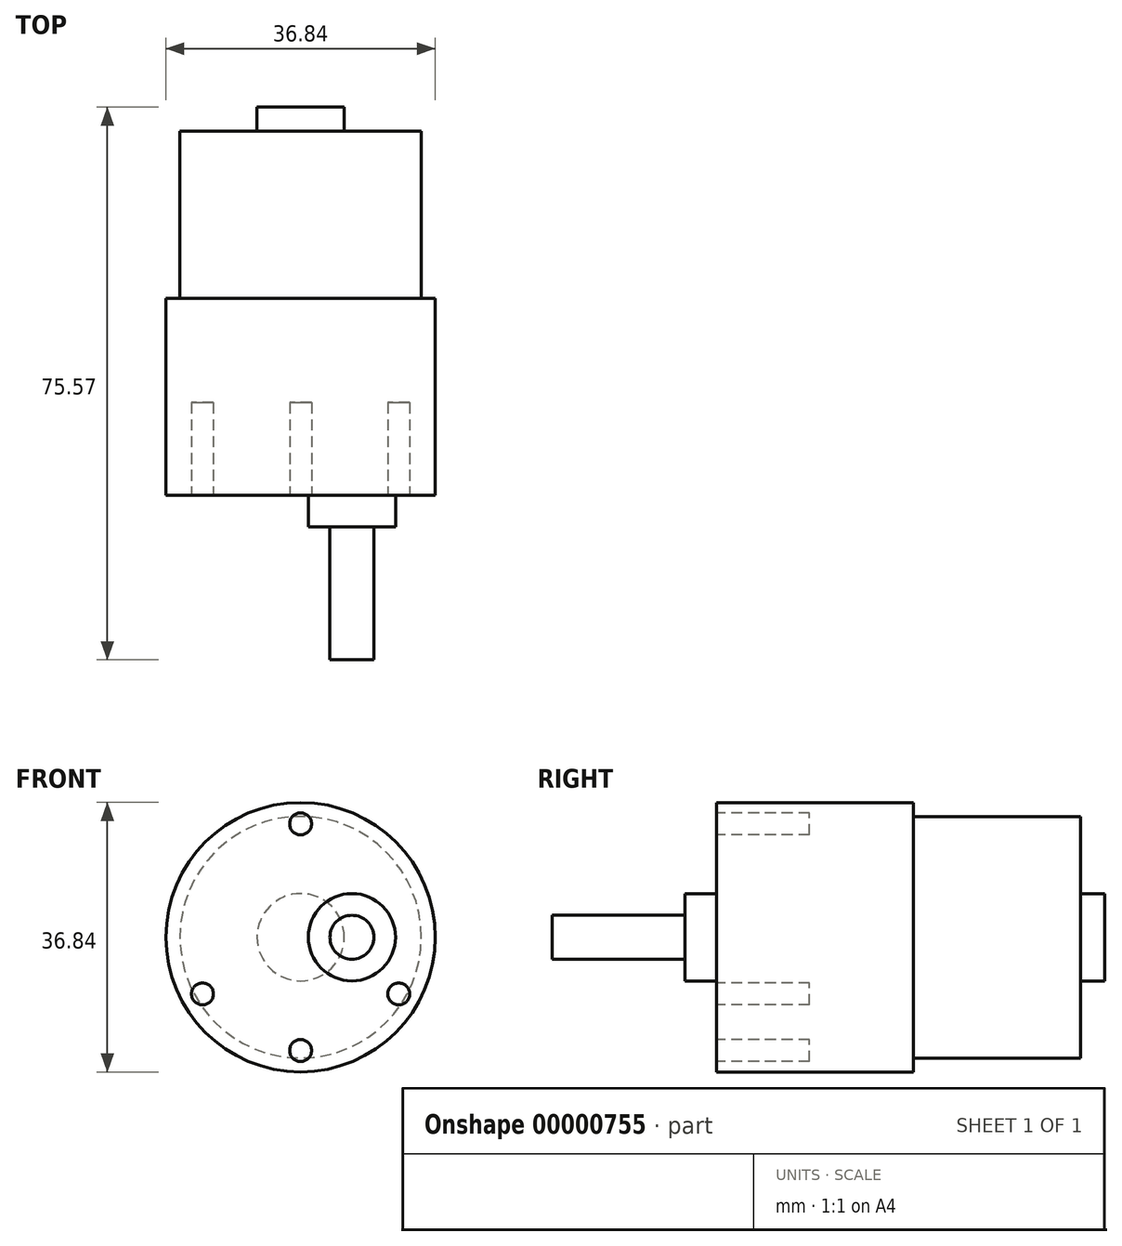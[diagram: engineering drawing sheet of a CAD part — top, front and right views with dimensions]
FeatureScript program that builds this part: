
annotation { "Feature Type Name" : "Feature", "Feature Type Description" : "" }
export const myFeature = defineFeature(function(context is Context, id is Id, definition is map)
    precondition{}
    {
        {
            var Q0;
            Q0=qCreatedBy(makeId("Top.planeOp"),FACE);
            var sketch = newSketch(context, id + "F0", { "sketchPlane" : qUnion([Q0])});
            skLineSegment(sketch, "E0", {"start": v(0, 0) * mm, "end": v(0, -75.57) * mm});
            skLineSegment(sketch, "E1", {"start": v(0, -75.57) * mm, "end": v(-3, -75.57) * mm});
            skLineSegment(sketch, "E2", {"start": v(-3, -75.57) * mm, "end": v(-3, -57.4) * mm});
            skLineSegment(sketch, "E3", {"start": v(-3, -57.4) * mm, "end": v(-5.97, -57.4) * mm});
            skLineSegment(sketch, "E4", {"start": v(-5.97, -57.4) * mm, "end": v(-5.97, -53.09) * mm});
            skLineSegment(sketch, "E5", {"start": v(-5.97, -53.09) * mm, "end": v(-18.41, -53.09) * mm});
            skLineSegment(sketch, "E6", {"start": v(-18.41, -53.09) * mm, "end": v(-18.41, -26.16) * mm});
            skLineSegment(sketch, "E7", {"start": v(-18.41, -26.16) * mm, "end": v(-16.5, -26.16) * mm});
            skLineSegment(sketch, "E8", {"start": v(-16.5, -26.16) * mm, "end": v(-16.51, -3.3) * mm});
            skLineSegment(sketch, "E9", {"start": v(-16.51, -3.3) * mm, "end": v(-5.97, -3.3) * mm});
            skLineSegment(sketch, "E10", {"start": v(-5.97, -3.3) * mm, "end": v(-5.97, 0) * mm});
            skLineSegment(sketch, "E11", {"start": v(-5.97, 0) * mm, "end": v(0, 0) * mm});
            skLineSegment(sketch, "E12", {"start": v(-5.97, -53.09) * mm, "end": v(0, -53.09) * mm});
            skSolve(sketch);
        }
        {
            var Q0;
            Q0=makeQuery(id+"F0.imprint","IMPRINT",FACE,{"disambiguationData":[TD([[makeQuery(id+"F0.imprint","IMPRINT",EDGE,{"derivedFrom":sQuery(id+"F0.wireOp",EDGE,"E5")}),-1.0]])]});
            var Q1;
            Q1=sQuery(id+"F0.wireOp",EDGE,"E0");
            revolve(context, id + "F1", {"entities" : qUnion([Q0]), "axis" : qUnion([Q1]), "revolveType" : RevolveType.FULL});
        }
        {
            var Q0;
            Q0=makeQuery(id+"F1.opRevolve","SWEPT_FACE",FACE,{"disambiguationData":[OSD([sQuery(id+"F0.wireOp",EDGE,"E5"),sQuery(id+"F0.wireOp",EDGE,"E12")])]});
            var sketch = newSketch(context, id + "F2", { "sketchPlane" : qUnion([Q0])});
            skCircle(sketch, "E13", {"center": v(7.01, 0) * mm, "radius": 5.97 * mm});
            skCircle(sketch, "E14", {"center": v(7.01, 0) * mm, "radius": 3 * mm});
            skSolve(sketch);
        }
        {
            var Q0;
            Q0=makeQuery(id+"F2.imprint","IMPRINT",FACE,{"disambiguationData":[TD([[makeQuery(id+"F2.imprint","IMPRINT",EDGE,{"derivedFrom":sQuery(id+"F2.wireOp",EDGE,"E13")}),1.0]])]});
            var Q1;
            Q1=makeQuery(id+"F2.imprint","IMPRINT",FACE,{"disambiguationData":[TD([[makeQuery(id+"F2.imprint","IMPRINT",EDGE,{"derivedFrom":sQuery(id+"F2.wireOp",EDGE,"E14")}),1.0]])]});
            extrude(context, id + "F3", {"entities" : qUnion([Q0, Q1]), "operationType" : NewBodyOperationType.ADD, "depth" : 4.32 * mm});
        }
        {
            var Q0;
            Q0=makeQuery(id+"F2.imprint","IMPRINT",FACE,{"disambiguationData":[TD([[makeQuery(id+"F2.imprint","IMPRINT",EDGE,{"derivedFrom":sQuery(id+"F2.wireOp",EDGE,"E14")}),1.0]])]});
            var Q1;
            Q1=sQuery(id+"F2.wireOp",EDGE,"E14");
            extrude(context, id + "F4", {"entities" : qUnion([Q0]), "operationType" : NewBodyOperationType.ADD, "surfaceEntities" : qUnion([Q1]), "depth" : 22.48 * mm});
        }
        {
            var Q0;
            Q0=makeQuery(id+"F2.imprint","IMPRINT",FACE,{"disambiguationData":[TD([[makeQuery(id+"F2.imprint","IMPRINT",EDGE,{"derivedFrom":sQuery(id+"F2.wireOp",EDGE,"E13")}),-1.0]])]});
            var sketch = newSketch(context, id + "F5", { "sketchPlane" : qUnion([Q0])});
            skCircle(sketch, "E15", {"center": v(-13.42, -7.76) * mm, "radius": 1.5 * mm});
            skCircle(sketch, "E16", {"center": v(0, 15.5) * mm, "radius": 1.5 * mm});
            skCircle(sketch, "E17", {"center": v(0, -15.5) * mm, "radius": 1.5 * mm});
            skCircle(sketch, "E18", {"center": v(13.42, -7.76) * mm, "radius": 1.5 * mm});
            skLineSegment(sketch, "E19", {"start": v(13.42, -7.76) * mm, "end": v(-13.42, -7.76) * mm, "construction": true});
            skLineSegment(sketch, "E20", {"start": v(0, 0) * mm, "end": v(0, -7.76) * mm, "construction": true});
            skLineSegment(sketch, "E21", {"start": v(0, 15.5) * mm, "end": v(0, -15.5) * mm, "construction": true});
            skSolve(sketch);
        }
        {
            var Q0;
            {Q0=qUnion([makeQuery(id+"F5.imprint","IMPRINT",FACE,{"disambiguationData":[TD([[makeQuery(id+"F5.imprint","IMPRINT",EDGE,{"derivedFrom":sQuery(id+"F5.wireOp",EDGE,"E15")}),1.0]])]}),makeQuery(id+"F5.imprint","IMPRINT",FACE,{"disambiguationData":[TD([[makeQuery(id+"F5.imprint","IMPRINT",EDGE,{"derivedFrom":sQuery(id+"F5.wireOp",EDGE,"E16")}),1.0]])]}),makeQuery(id+"F5.imprint","IMPRINT",FACE,{"disambiguationData":[TD([[makeQuery(id+"F5.imprint","IMPRINT",EDGE,{"derivedFrom":sQuery(id+"F5.wireOp",EDGE,"E17")}),1.0]])]}),makeQuery(id+"F5.imprint","IMPRINT",FACE,{"disambiguationData":[TD([[makeQuery(id+"F5.imprint","IMPRINT",EDGE,{"derivedFrom":sQuery(id+"F5.wireOp",EDGE,"E18")}),1.0]])]})]);}
            extrude(context, id + "F6", {"entities" : qUnion([Q0]), "operationType" : NewBodyOperationType.REMOVE, "oppositeDirection" : true, "depth" : 12.7 * mm});
        }
    });
